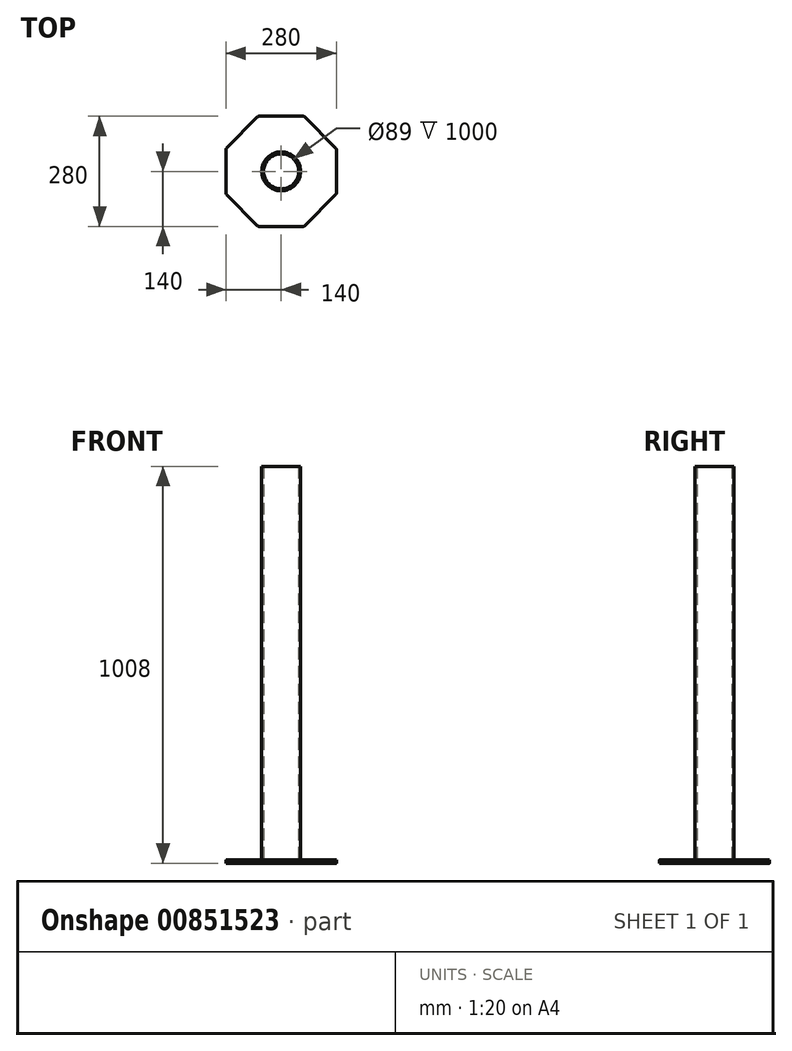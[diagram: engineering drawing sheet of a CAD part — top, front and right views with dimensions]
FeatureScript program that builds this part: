
annotation { "Feature Type Name" : "Feature", "Feature Type Description" : "" }
export const myFeature = defineFeature(function(context is Context, id is Id, definition is map)
    precondition{}
    {
        {
            var Q0;
            Q0=qCreatedBy(makeId("Top.planeOp"),FACE);
            var sketch = newSketch(context, id + "F0", { "sketchPlane" : qUnion([Q0])});
            skCircle(sketch, "E0.cCircle", {"center": v(0, 0) * mm, "radius": 140 * mm, "construction": true});
            skLineSegment(sketch, "E0.0", {"start": v(-57.99, 140) * mm, "end": v(57.99, 140) * mm});
            skLineSegment(sketch, "E0.1", {"start": v(57.99, 140) * mm, "end": v(140, 57.99) * mm});
            skLineSegment(sketch, "E0.2", {"start": v(140, 57.99) * mm, "end": v(140, -57.99) * mm});
            skLineSegment(sketch, "E0.3", {"start": v(140, -57.99) * mm, "end": v(57.99, -140) * mm});
            skLineSegment(sketch, "E0.4", {"start": v(57.99, -140) * mm, "end": v(-57.99, -140) * mm});
            skLineSegment(sketch, "E0.5", {"start": v(-57.99, -140) * mm, "end": v(-140, -57.99) * mm});
            skLineSegment(sketch, "E0.6", {"start": v(-140, -57.99) * mm, "end": v(-140, 57.99) * mm});
            skLineSegment(sketch, "E0.7", {"start": v(-140, 57.99) * mm, "end": v(-57.99, 140) * mm});
            skPoint(sketch, "E0.0.midPoint", {"position": v(0, 140) * mm});
            skSolve(sketch);
        }
        {
            var Q0;
            Q0 = qSketchRegion(id + "F0", true);
            extrude(context, id + "F1", {"entities" : qUnion([Q0]), "depth" : 8 * mm, "offsetDistance" : 25 * mm});
        }
        {
            var Q0;
            Q0=makeQuery(id+"F1.opExtrude","CAP_FACE",FACE,{"disambiguationData":[OSD([sQuery(id+"F0.wireOp",EDGE,"E0.0"),sQuery(id+"F0.wireOp",EDGE,"E0.1"),sQuery(id+"F0.wireOp",EDGE,"E0.2"),sQuery(id+"F0.wireOp",EDGE,"E0.3"),sQuery(id+"F0.wireOp",EDGE,"E0.4"),sQuery(id+"F0.wireOp",EDGE,"E0.5"),sQuery(id+"F0.wireOp",EDGE,"E0.6"),sQuery(id+"F0.wireOp",EDGE,"E0.7")])],"isStart":false});
            var sketch = newSketch(context, id + "F2", { "sketchPlane" : qUnion([Q0])});
            skCircle(sketch, "E1", {"center": v(0, 0) * mm, "radius": 49.5 * mm});
            skCircle(sketch, "E2.0", {"center": v(0, 0) * mm, "radius": 44.5 * mm});
            skSolve(sketch);
        }
        {
            var Q0;
            Q0 = qSketchRegion(id + "F2", true);
            extrude(context, id + "F3", {"entities" : qUnion([Q0]), "operationType" : NewBodyOperationType.ADD, "depth" : 1000 * mm, "offsetDistance" : 25 * mm});
        }
        {
            var Q0;
            Q0=makeQuery(id+"F1.opExtrude","SWEPT_EDGE",EDGE,{"disambiguationData":[OSD([sQuery(id+"F0.wireOp",EDGE,"E0.0"),sQuery(id+"F0.wireOp",EDGE,"E0.1")])]});
            var Q1;
            Q1=makeQuery(id+"F1.opExtrude","SWEPT_EDGE",EDGE,{"disambiguationData":[OSD([sQuery(id+"F0.wireOp",EDGE,"E0.0"),sQuery(id+"F0.wireOp",EDGE,"E0.7")])]});
            var Q2;
            Q2=makeQuery(id+"F1.opExtrude","SWEPT_EDGE",EDGE,{"disambiguationData":[OSD([sQuery(id+"F0.wireOp",EDGE,"E0.6"),sQuery(id+"F0.wireOp",EDGE,"E0.7")])]});
            var Q3;
            Q3=makeQuery(id+"F1.opExtrude","SWEPT_EDGE",EDGE,{"disambiguationData":[OSD([sQuery(id+"F0.wireOp",EDGE,"E0.5"),sQuery(id+"F0.wireOp",EDGE,"E0.6")])]});
            var Q4;
            Q4=makeQuery(id+"F1.opExtrude","SWEPT_EDGE",EDGE,{"disambiguationData":[OSD([sQuery(id+"F0.wireOp",EDGE,"E0.4"),sQuery(id+"F0.wireOp",EDGE,"E0.5")])]});
            var Q5;
            Q5=makeQuery(id+"F1.opExtrude","SWEPT_EDGE",EDGE,{"disambiguationData":[OSD([sQuery(id+"F0.wireOp",EDGE,"E0.3"),sQuery(id+"F0.wireOp",EDGE,"E0.4")])]});
            var Q6;
            Q6=makeQuery(id+"F1.opExtrude","SWEPT_EDGE",EDGE,{"disambiguationData":[OSD([sQuery(id+"F0.wireOp",EDGE,"E0.2"),sQuery(id+"F0.wireOp",EDGE,"E0.3")])]});
            var Q7;
            Q7=makeQuery(id+"F1.opExtrude","SWEPT_EDGE",EDGE,{"disambiguationData":[OSD([sQuery(id+"F0.wireOp",EDGE,"E0.1"),sQuery(id+"F0.wireOp",EDGE,"E0.2")])]});
            fillet(context, id + "F4", {"entities" : qUnion([Q0, Q1, Q2, Q3, Q4, Q5, Q6, Q7]), "radius" : 5 * mm, "tangentPropagation" : true, "allowEdgeOverflow" : false});
        }
    });
